# Revit family: Sofiero-Bar-Collection-OM
name_source: partatom
category: Furniture
units: mm (PartAtom-declared; Revit-internal decimal feet)

## family parameters
Always vertical = Yes
Cut with Voids When Loaded = No
OmniClass Number = 23.21.23.13.15
Room Calculation Point = No
Shared = No
Work Plane-Based = No

## types (4) — shared parameters
BIMobject category = Other Furniture
Description = Bargrupp Sofiero Above Ground
Edition number = 1
IFC Classification = Object
Manufacturer = Hags
Manufacturer name = HAGS
OmniClass Code = 23-11 27 00
OmniClass Description = Landscaping
Product Guid = b0cd4f6b-1338-45be-8a70-5679c3d9deb8
Product SKU = Bargrupp_Sofiero_Above_Ground
Product data url = https://bimobject.com
Product name = Sofiero Barmöbler
QR code = https://bimobject.com
URL = https://www.hags.com
Uniclass 1.4 Code = JN
Uniclass 1.4 Description = Furniture/Equipment
zero-valued in all types: Default Elevation

## per-type parameters (varying)
| type | Body material | Body material_90 | Construction material | Model | Product url |
| 8077452 Bark Brown / Black | Hags - Wood - Bark brown | Hags - Wood - Bark brown 90 | Hags - Steel - Powder coated - Black | 8077452 | https://hags.se |
| 8077453 Tan / Galvanized | Hags - Wood - Tan | Hags - Wood - Tan 90 | Hags - Steel - Galvanized | 8077453 | https://hags.se |
| 8097656 Hardwood / Galvanized | Hags - Hard Wood | Hags - Hard Wood | Hags - Steel - Galvanized | 8097656 | https://www.hags.com |
| 8097657 Hardwood / Black | Hags - Hard Wood | Hags - Hard Wood | Hags - Steel - Powder coated - Black | 8097657 | https://www.hags.com |

## geometry (parser evidence)
native form markers: Sweep x4
no freeform markers — native parametric forms only
